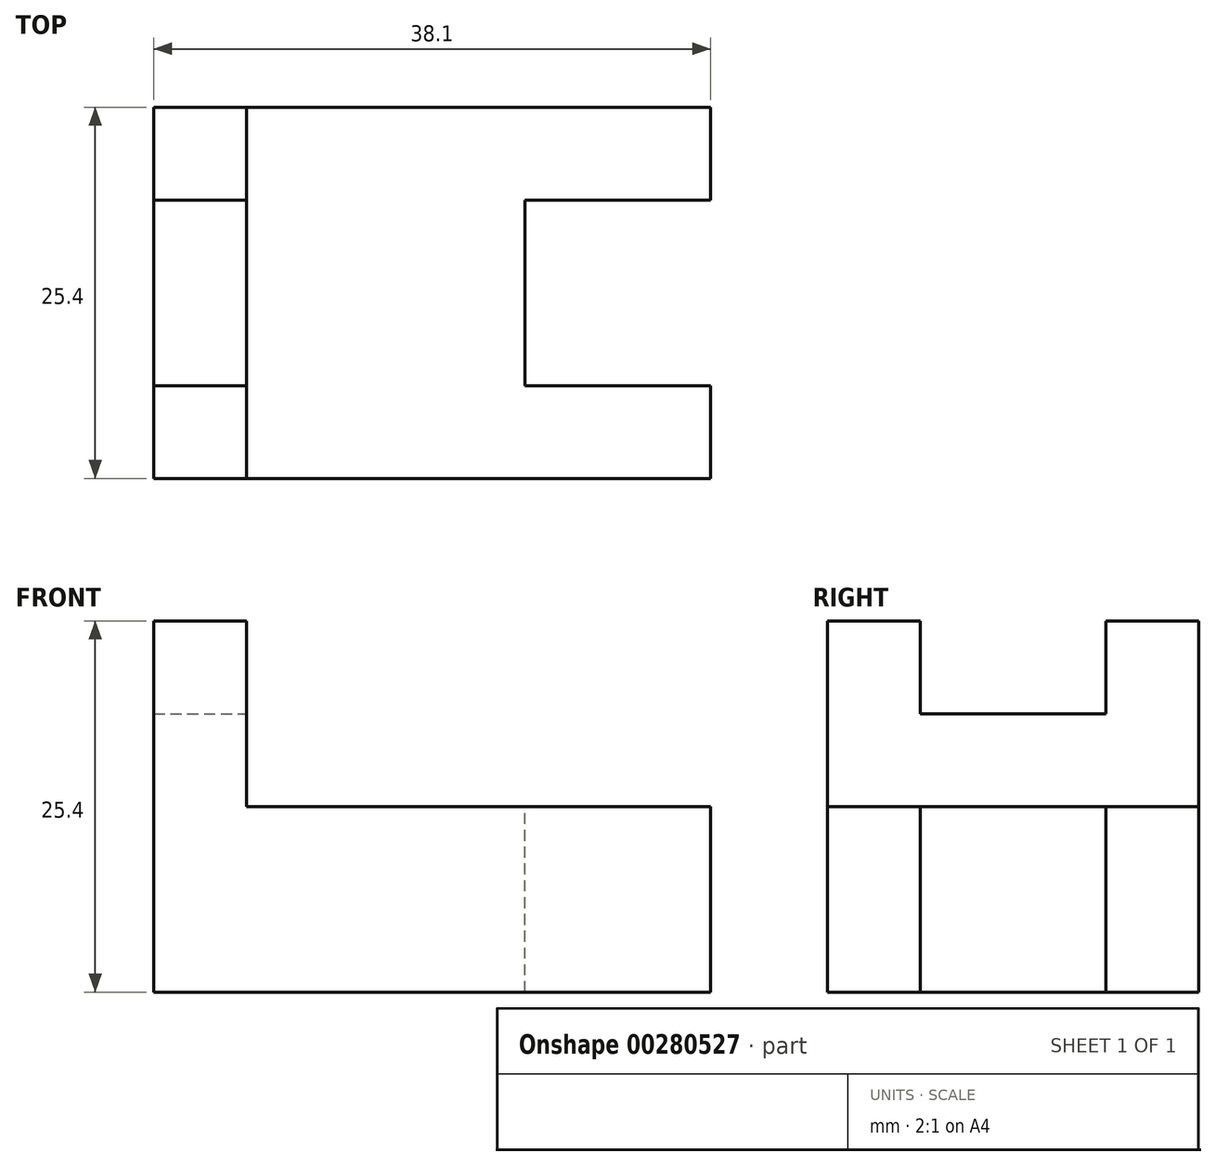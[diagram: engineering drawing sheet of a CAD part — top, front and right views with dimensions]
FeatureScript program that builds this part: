
annotation { "Feature Type Name" : "Feature", "Feature Type Description" : "" }
export const myFeature = defineFeature(function(context is Context, id is Id, definition is map)
    precondition{}
    {
        {
            var Q0;
            Q0=qCreatedBy(makeId("Front.planeOp"),FACE);
            var sketch = newSketch(context, id + "F0", { "sketchPlane" : qUnion([Q0])});
            skLineSegment(sketch, "E0", {"start": v(0, 0) * mm, "end": v(38.1, 0) * mm});
            skLineSegment(sketch, "E1", {"start": v(38.1, 0) * mm, "end": v(38.1, 12.7) * mm});
            skLineSegment(sketch, "E2", {"start": v(38.1, 12.7) * mm, "end": v(6.35, 12.7) * mm});
            skLineSegment(sketch, "E3", {"start": v(6.35, 12.7) * mm, "end": v(6.35, 25.4) * mm});
            skLineSegment(sketch, "E4", {"start": v(6.35, 25.4) * mm, "end": v(0, 25.4) * mm});
            skLineSegment(sketch, "E5", {"start": v(0, 25.4) * mm, "end": v(0, 0) * mm});
            skSolve(sketch);
        }
        {
            var Q0;
            Q0 = qSketchRegion(id + "F0", true);
            extrude(context, id + "F1", {"entities" : qUnion([Q0]), "endBound" : BoundingType.SYMMETRIC, "depth" : 25.4 * mm});
        }
        {
            var Q0;
            Q0=qCreatedBy(makeId("Front.planeOp"),FACE);
            var sketch = newSketch(context, id + "F2", { "sketchPlane" : qUnion([Q0])});
            skLineSegment(sketch, "E6.bottom", {"start": v(0, 25.4) * mm, "end": v(6.35, 25.4) * mm});
            skLineSegment(sketch, "E6.top", {"start": v(0, 19.05) * mm, "end": v(6.35, 19.05) * mm});
            skLineSegment(sketch, "E6.left", {"start": v(0, 25.4) * mm, "end": v(0, 19.05) * mm});
            skLineSegment(sketch, "E6.right", {"start": v(6.35, 25.4) * mm, "end": v(6.35, 19.05) * mm});
            skSolve(sketch);
        }
        {
            var Q0;
            Q0 = qSketchRegion(id + "F2", true);
            extrude(context, id + "F3", {"entities" : qUnion([Q0]), "operationType" : NewBodyOperationType.REMOVE, "endBound" : BoundingType.SYMMETRIC, "depth" : 12.7 * mm});
        }
        {
            var Q0;
            Q0=qCreatedBy(makeId("Front.planeOp"),FACE);
            var sketch = newSketch(context, id + "F4", { "sketchPlane" : qUnion([Q0])});
            skLineSegment(sketch, "E7.bottom", {"start": v(38.1, 0) * mm, "end": v(25.4, 0) * mm});
            skLineSegment(sketch, "E7.top", {"start": v(38.1, 12.7) * mm, "end": v(25.4, 12.7) * mm});
            skLineSegment(sketch, "E7.left", {"start": v(38.1, 0) * mm, "end": v(38.1, 12.7) * mm});
            skLineSegment(sketch, "E7.right", {"start": v(25.4, 0) * mm, "end": v(25.4, 12.7) * mm});
            skSolve(sketch);
        }
        {
            var Q0;
            Q0 = qSketchRegion(id + "F4", true);
            extrude(context, id + "F5", {"entities" : qUnion([Q0]), "operationType" : NewBodyOperationType.REMOVE, "endBound" : BoundingType.SYMMETRIC, "oppositeDirection" : true, "depth" : 12.7 * mm});
        }
    });
